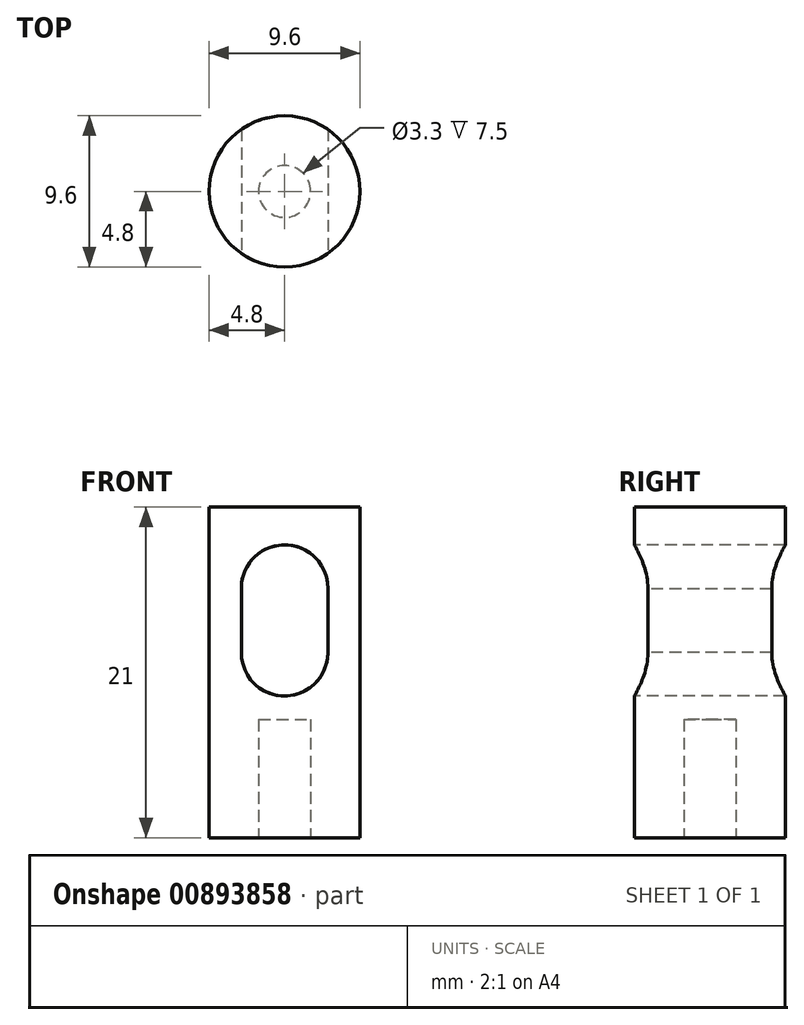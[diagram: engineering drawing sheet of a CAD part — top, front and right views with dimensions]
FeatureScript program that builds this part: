
annotation { "Feature Type Name" : "Feature", "Feature Type Description" : "" }
export const myFeature = defineFeature(function(context is Context, id is Id, definition is map)
    precondition{}
    {
        {
            var Q0;
            Q0=qCreatedBy(makeId("Top.planeOp"),FACE);
            var sketch = newSketch(context, id + "F0", { "sketchPlane" : qUnion([Q0])});
            skCircle(sketch, "E0", {"center": v(0, 0) * mm, "radius": 4.8 * mm});
            skSolve(sketch);
        }
        {
            var Q0;
            Q0 = qSketchRegion(id + "F0", true);
            extrude(context, id + "F1", {"entities" : qUnion([Q0]), "depth" : 21 * mm, "offsetDistance" : 25 * mm});
        }
        {
            var Q0;
            Q0=makeQuery(id+"F1.opExtrude","CAP_FACE",FACE,{"disambiguationData":[OSD([sQuery(id+"F0.wireOp",EDGE,"E0")])],"isStart":true});
            var sketch = newSketch(context, id + "F2", { "sketchPlane" : qUnion([Q0])});
            skCircle(sketch, "E1", {"center": v(0, 0) * mm, "radius": 1.65 * mm});
            skSolve(sketch);
        }
        {
            var Q0;
            Q0 = qSketchRegion(id + "F2", true);
            extrude(context, id + "F3", {"entities" : qUnion([Q0]), "operationType" : NewBodyOperationType.REMOVE, "oppositeDirection" : true, "depth" : 7.5 * mm, "offsetDistance" : 25 * mm});
        }
        {
            var Q0;
            Q0=qCreatedBy(makeId("Front.planeOp"),FACE);
            var sketch = newSketch(context, id + "F4", { "sketchPlane" : qUnion([Q0])});
            skArc(sketch, "E2", {"start": v(2.75, 15.81) * mm, "mid": v(0.02, 18.6) * mm, "end": v(-2.75, 15.85) * mm});
            skArc(sketch, "E3", {"start": v(-2.75, 11.78) * mm, "mid": v(-0.02, 9) * mm, "end": v(2.75, 11.75) * mm});
            skLineSegment(sketch, "E4", {"start": v(2.75, 15.89) * mm, "end": v(2.75, 11.75) * mm});
            skLineSegment(sketch, "E5", {"start": v(-2.75, 11.72) * mm, "end": v(-2.75, 15.85) * mm});
            skSolve(sketch);
        }
        {
            var Q0;
            Q0 = qSketchRegion(id + "F4", true);
            extrude(context, id + "F5", {"entities" : qUnion([Q0]), "operationType" : NewBodyOperationType.REMOVE, "endBound" : BoundingType.UP_TO_NEXT, "oppositeDirection" : true, "depth" : 25 * mm, "offsetDistance" : 25 * mm, "hasSecondDirection" : true, "secondDirectionBound" : SecondDirectionBoundingType.UP_TO_NEXT, "secondDirectionOppositeDirection" : false, "secondDirectionDepth" : 25 * mm});
        }
    });
